# Revit family: GR2013027 ZENTRAL MAMPARA DE VIDRIO
name_source: partatom
category: Plumbing Fixtures
revit_build: Autodesk Revit 2017 (Build: 20160225_1515(x64)
units: mm (PartAtom-declared; Revit-internal decimal feet)

## family parameters
Always vertical = Yes
Cut with Voids When Loaded = No
OmniClass Number = 23.45.00.00
OmniClass Title = Sanitary, Laundry, and Cleaning Equipment
Part Type = Normal
Room Calculation Point = No
Round Connector Dimension = Use Diameter
Shared = No
Work Plane-Based = No

## types (5) — shared parameters
Accesories Material = Chrome_Finish
Anti-Lime Treatment = FeelNet 3D Included
Assembly Code = C1030200
BIMobject category = Shower screens
Brand url = http://www.duscholux.es
Certified Quality TÜV Certification = http://www.duscholux.es
Certified Quality UNE EN 14428 = http://www.duscholux.es
Combinations = Lateral 90°
Components = Eropean components
Configuration enclosure = http://configuratumampara.duscholux.es
Description = 2 fixed segments + slider twin doors for bath
Edition number = 1
Environmental Management ISO 14001 = ECOEMBES Certificate
Fact sheet = http://www.duscholux.es
Frame Material = Platinum Aluminium Finish
Glass Material = Glass_Material-Duscholux
Glass in Building UNE EN 12150 = CE Conformity marking
Handle Height = 800 mm  [stored 2.62467 ft]
Handle Material = Chrome_Finish
Height = 1850 mm  [stored 6.06955 ft]
Image = http://www.duscholux.es
Installation instructions = https://
Maintenance and Cleaning = http://www.duscholux.es
Manufacturer = Duscholux Ibérica, S.A.
Manufacturer country = Spain
Manufacturer name = Duscholux
Material main = Glass
Material secondary = Aluminium
Max Height = 2000 mm  [stored 6.56168 ft]
Nominal height = 1600
Opening System = Sliding
Opening System Image = http://www.duscholux.es
Optional = Towel rail / Shelf
Product Guid = 0aaea0e6-c2a2-40d4-bf91-71c394719ea9
Product SKU = DUSCHOGRAVITY_2FIJOS_2PUERTAS_BANERA
Product certification = http://www.duscholux.es
Product data url = https://bimobject.com
Product family = Shower enclosure
Product group = Duscho Gravity
Product url = http://www.duscholux.es
Products = http://www.duscholux.es
QR code = http://bimobject.com
Ref. = KAW
Series = DuschoGravity
Technical description = http://www.duscholux.es
Thickness Safety Glass Fixed Panel = 8 mm  [stored 0.0262467 ft]
Thickness Safety Glass Sliding = 5 mm  [stored 0.0164042 ft]
URL = http://www.duscholux.es
Weight Net (Kg) = 44.7
Youtube clip = http://www.duscholux.es
zero-valued in all types: Bath Height, Nominal width, Opening Door, Opening Percentage

## per-type parameters (varying)
| type | Min Max Width | Sliding Door Width | Width |
| 140x185 | 1400 mm  [stored 4.59318 ft] | 356 mm | 1400 mm  [stored 4.59318 ft] |
| 150x185 | 1500 mm  [stored 4.92126 ft] | 381 mm | 1500 mm  [stored 4.92126 ft] |
| 160x185 | 1600 mm  [stored 5.24934 ft] | 406 mm | 1600 mm  [stored 5.24934 ft] |
| 170x185 | 1700 mm  [stored 5.57743 ft] | 431 mm | 1700 mm  [stored 5.57743 ft] |
| 180x185 | 1800 mm  [stored 5.90551 ft] | 456 mm | 1800 mm  [stored 5.90551 ft] |

note: [stored X ft] marks values corroborated as IEEE doubles in the binary element streams (Revit-internal decimal feet)
